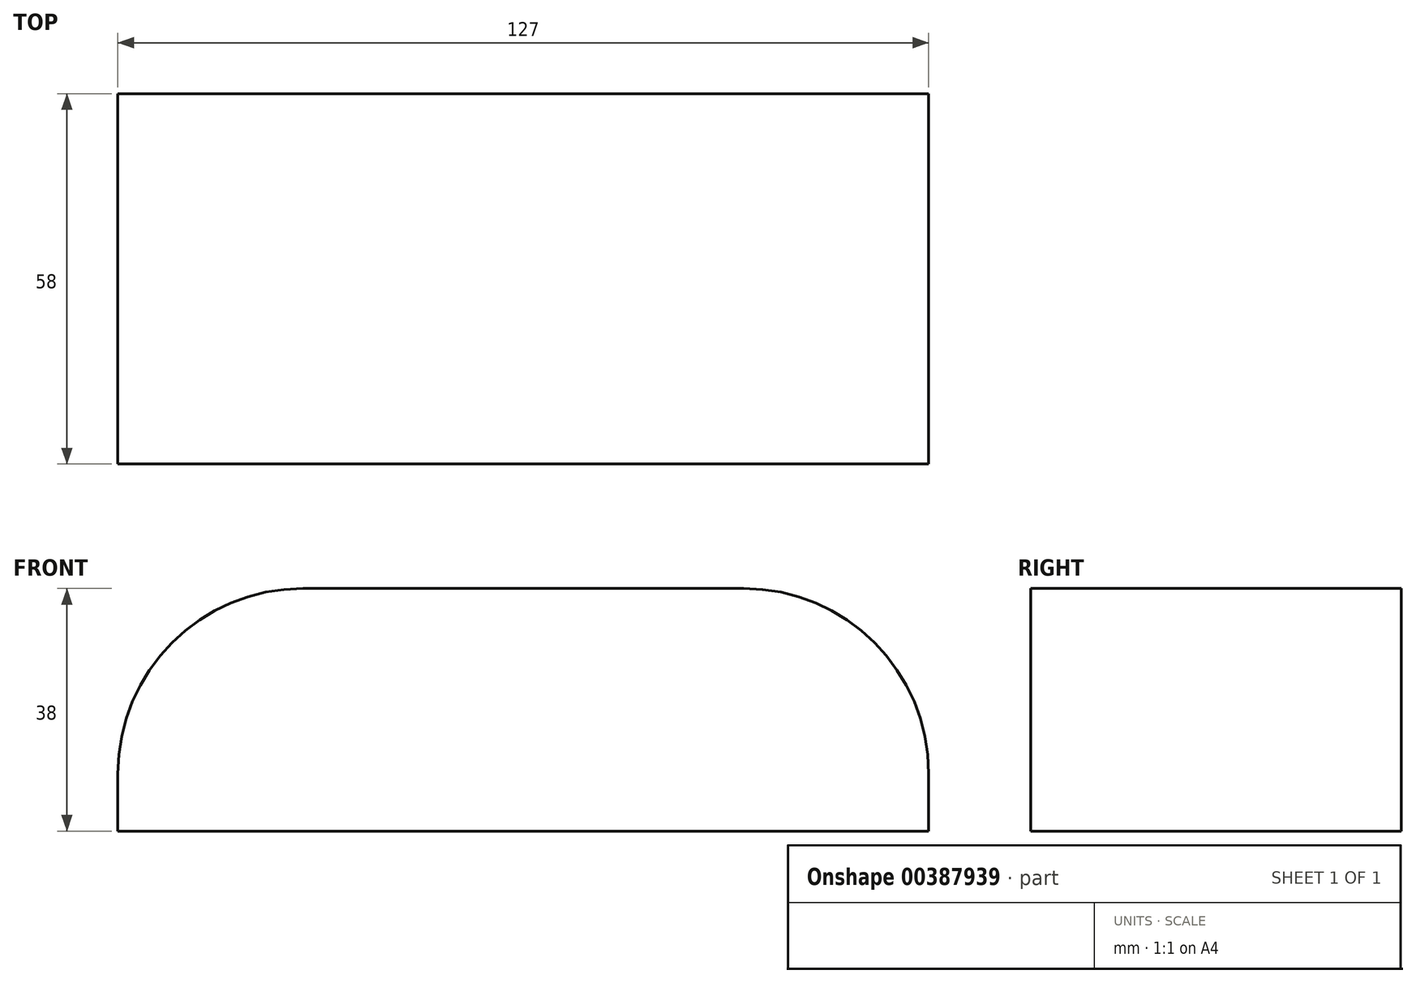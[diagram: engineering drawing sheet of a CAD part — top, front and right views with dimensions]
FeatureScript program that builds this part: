
annotation { "Feature Type Name" : "Feature", "Feature Type Description" : "" }
export const myFeature = defineFeature(function(context is Context, id is Id, definition is map)
    precondition{}
    {
        {
            var Q0;
            Q0=qCreatedBy(makeId("Front.planeOp"),FACE);
            var sketch = newSketch(context, id + "F0", { "sketchPlane" : qUnion([Q0])});
            skLineSegment(sketch, "E0.bottom", {"start": v(63.5, 0) * mm, "end": v(-63.5, 0) * mm});
            skLineSegment(sketch, "E0.top", {"start": v(34.5, 38) * mm, "end": v(-34.5, 38) * mm});
            skLineSegment(sketch, "E0.left", {"start": v(63.5, 0) * mm, "end": v(63.5, 9) * mm});
            skLineSegment(sketch, "E0.right", {"start": v(-63.5, 0) * mm, "end": v(-63.5, 9) * mm});
            skPoint(sketch, "E1.visualSharp", {"position": v(-63.5, 38) * mm});
            skArc(sketch, "E1.filletArc", {"start": v(-34.5, 38) * mm, "mid": v(-55, 29.5) * mm, "end": v(-63.5, 9) * mm});
            skPoint(sketch, "E2.visualSharp", {"position": v(63.5, 38) * mm});
            skArc(sketch, "E2.filletArc", {"start": v(63.5, 9) * mm, "mid": v(55, 29.5) * mm, "end": v(34.5, 38) * mm});
            skSolve(sketch);
        }
        {
            var Q0;
            Q0=makeQuery(id+"F0.imprint","IMPRINT",FACE,{"disambiguationData":[TD([[makeQuery(id+"F0.imprint","IMPRINT",EDGE,{"derivedFrom":sQuery(id+"F0.wireOp",EDGE,"E0.bottom")}),-1.0]])]});
            extrude(context, id + "F1", {"entities" : qUnion([Q0]), "endBound" : BoundingType.SYMMETRIC, "depth" : 58 * mm});
        }
    });
